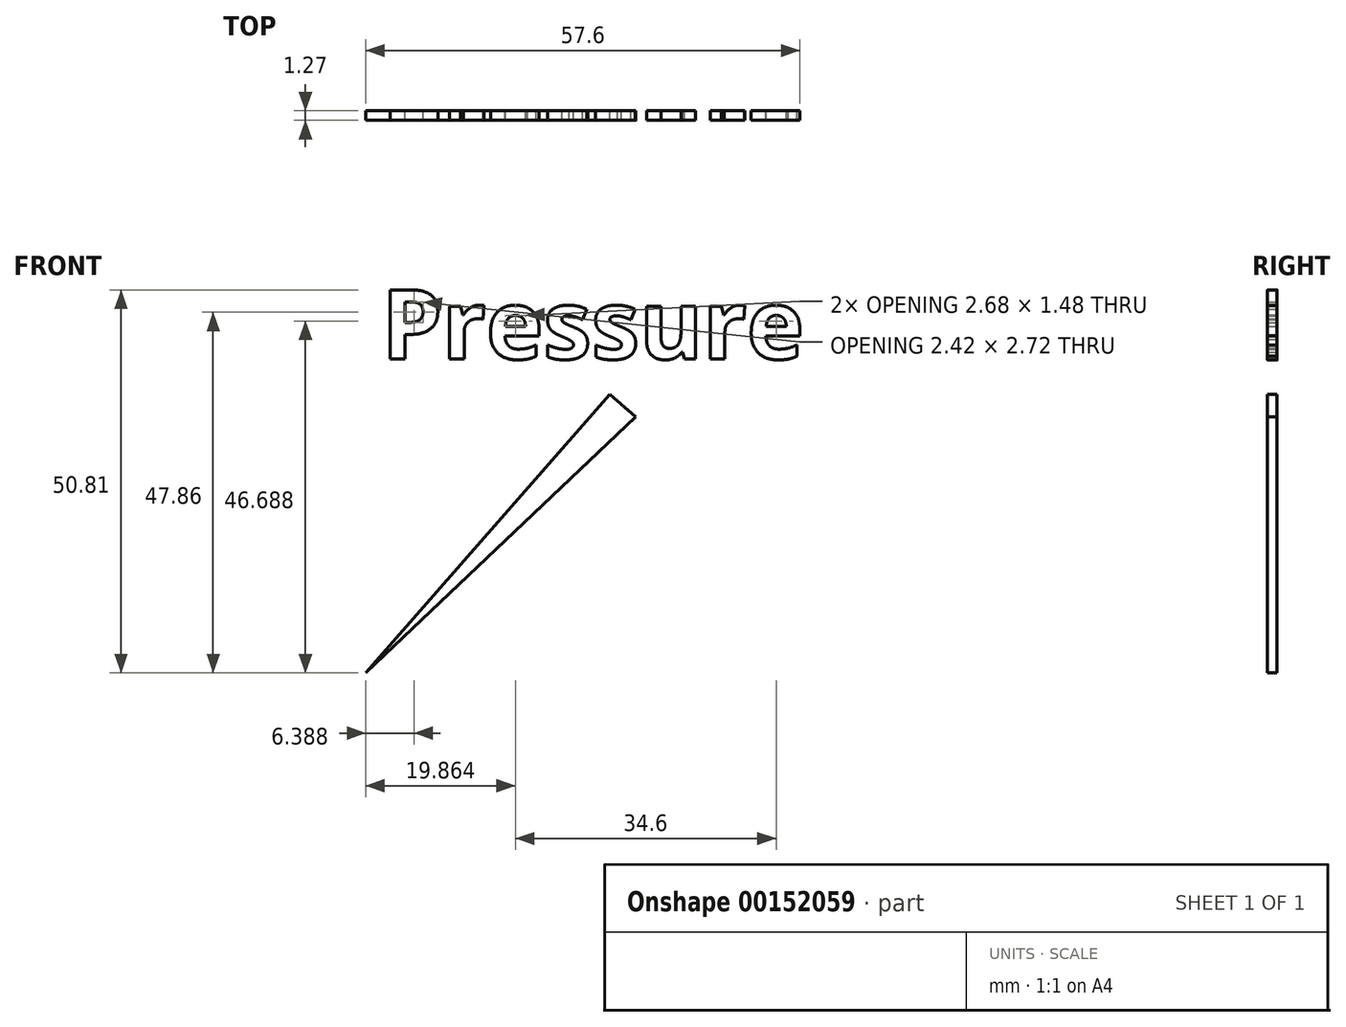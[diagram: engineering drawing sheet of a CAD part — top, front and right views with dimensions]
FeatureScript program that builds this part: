
annotation { "Feature Type Name" : "Feature", "Feature Type Description" : "" }
export const myFeature = defineFeature(function(context is Context, id is Id, definition is map)
    precondition{}
    {
        {
            var Q0;
            Q0=qCreatedBy(makeId("Front.planeOp"),FACE);
            var sketch = newSketch(context, id + "F0", { "sketchPlane" : qUnion([Q0])});
            skLineSegment(sketch, "E0", {"start": v(-30.28, -31.69) * mm, "end": v(2.13, 5.25) * mm});
            skLineSegment(sketch, "E1", {"start": v(2.13, 5.25) * mm, "end": v(5.5, 2.3) * mm});
            skLineSegment(sketch, "E2", {"start": v(5.5, 2.3) * mm, "end": v(-30.28, -31.69) * mm});
            skText(sketch, "E3", { "text": "Pressure", "fontName": "OpenSans-Bold.ttf"});
            const initialGuessF0  = {"E3": [-0.0282, 0.00996, 1, 0, 0.00924]};
            skSetInitialGuess(sketch, initialGuessF0);
            skSolve(sketch);
        }
        {
            var Q0;
            Q0 = qSketchRegion(id + "F0", true);
            extrude(context, id + "F1", {"entities" : qUnion([Q0]), "depth" : 1.27 * mm});
        }
    });
